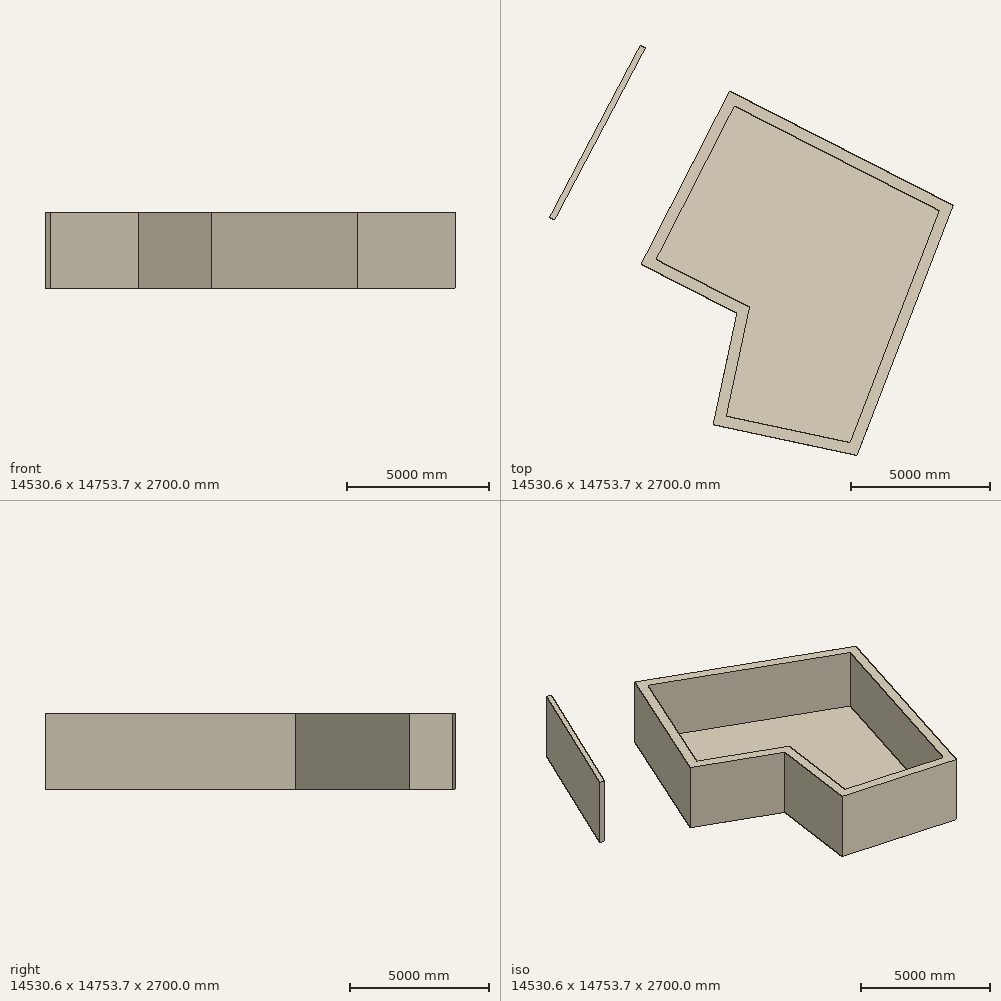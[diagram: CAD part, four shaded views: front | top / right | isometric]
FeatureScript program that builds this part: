
annotation { "Feature Type Name" : "Feature", "Feature Type Description" : "" }
export const myFeature = defineFeature(function(context is Context, id is Id, definition is map)
    precondition{}
    {
        {
            var Q0;
            Q0=qCreatedBy(makeId("Top.planeOp"),FACE);
            var sketch = newSketch(context, id + "F0", { "sketchPlane" : qUnion([Q0])});
            skLineSegment(sketch, "E0", {"start": v(0, 0) * mm, "end": v(-9470, -17950) * mm});
            skLineSegment(sketch, "E1", {"start": v(-9470, -17950) * mm, "end": v(3690, -24620) * mm});
            skLineSegment(sketch, "E2", {"start": v(3690, -24620) * mm, "end": v(11000, -5620) * mm});
            skLineSegment(sketch, "E3", {"start": v(11000, -5620) * mm, "end": v(0, 0) * mm});
            skSolve(sketch);
        }
        {
            var Q0;
            Q0=qCreatedBy(makeId("Top.planeOp"),FACE);
            var sketch = newSketch(context, id + "F1", { "sketchPlane" : qUnion([Q0])});
            skLineSegment(sketch, "E4", {"start": v(-1166.65, -2211.34) * mm, "end": v(10097.33, -7966.2) * mm});
            skLineSegment(sketch, "E5", {"start": v(10097.33, -7966.2) * mm, "end": v(6635.15, -16965.03) * mm});
            skLineSegment(sketch, "E6", {"start": v(6635.15, -16965.03) * mm, "end": v(1452.73, -15857.52) * mm});
            skLineSegment(sketch, "E7", {"start": v(1452.73, -15857.52) * mm, "end": v(2309.57, -11848.05) * mm});
            skLineSegment(sketch, "E8", {"start": v(2309.57, -11848.05) * mm, "end": v(-4433.27, -8403.08) * mm});
            skLineSegment(sketch, "E9", {"start": v(-4433.27, -8403.08) * mm, "end": v(-1166.65, -2211.34) * mm});
            skPoint(sketch, "E10.orphan", {"position": v(0, 0) * mm});
            skLineSegment(sketch, "E11", {"start": v(2048.08, -3853.77) * mm, "end": v(-1136.7, -10087.33) * mm});
            skLineSegment(sketch, "E12", {"start": v(2309.57, -11848.05) * mm, "end": v(3824.07, -4761.14) * mm});
            skLineSegment(sketch, "E13", {"start": v(1271.05, -16707.65) * mm, "end": v(5836.72, -19040.3) * mm});
            skSolve(sketch);
        }
        {
            var Q0;
            Q0=qCreatedBy(makeId("Top.planeOp"),FACE);
            var sketch = newSketch(context, id + "F2", { "sketchPlane" : qUnion([Q0])});
            skLineSegment(sketch, "E14", {"start": v(-1136.7, -10087.33) * mm, "end": v(2048.08, -3853.77) * mm});
            skLineSegment(sketch, "E15", {"start": v(2048.08, -3853.77) * mm, "end": v(10097.33, -7966.2) * mm});
            skLineSegment(sketch, "E16", {"start": v(10097.33, -7966.2) * mm, "end": v(6635.15, -16965.03) * mm});
            skLineSegment(sketch, "E17", {"start": v(6635.15, -16965.03) * mm, "end": v(1452.73, -15857.52) * mm});
            skLineSegment(sketch, "E18", {"start": v(1452.73, -15857.52) * mm, "end": v(2309.57, -11848.05) * mm});
            skLineSegment(sketch, "E19", {"start": v(2309.57, -11848.05) * mm, "end": v(-1136.7, -10087.33) * mm});
            skLineSegment(sketch, "E20", {"start": v(-4433.27, -8403.08) * mm, "end": v(-1166.65, -2211.34) * mm});
            skLineSegment(sketch, "E21", {"start": v(-1166.65, -2211.34) * mm, "end": v(-979.63, -2306.89) * mm});
            skLineSegment(sketch, "E22", {"start": v(-979.63, -2306.89) * mm, "end": v(-4246.24, -8498.63) * mm});
            skLineSegment(sketch, "E23", {"start": v(-4246.24, -8498.63) * mm, "end": v(-4433.27, -8403.08) * mm});
            skSolve(sketch);
        }
        {
            var Q0;
            Q0 = qSketchRegion(id + "F2", true);
            extrude(context, id + "F3", {"entities" : qUnion([Q0]), "oppositeDirection" : true, "depth" : 300 * mm});
        }
        {
            var Q0;
            Q0=qCreatedBy(makeId("Top.planeOp"),FACE);
            var sketch = newSketch(context, id + "F4", { "sketchPlane" : qUnion([Q0])});
            skLineSegment(sketch, "E24.0", {"start": v(2048.08, -3853.77) * mm, "end": v(-1136.7, -10087.33) * mm});
            skLineSegment(sketch, "E25.0", {"start": v(1452.73, -15857.52) * mm, "end": v(2309.57, -11848.05) * mm});
            skPoint(sketch, "E26.0", {"position": v(4043.94, -16411.27) * mm});
            skLineSegment(sketch, "E27.0", {"start": v(6635.15, -16965.03) * mm, "end": v(1452.73, -15857.52) * mm});
            skLineSegment(sketch, "E28.0", {"start": v(10097.33, -7966.2) * mm, "end": v(6635.15, -16965.03) * mm});
            skLineSegment(sketch, "E29.0", {"start": v(-979.63, -2306.89) * mm, "end": v(-4246.24, -8498.63) * mm});
            skLineSegment(sketch, "E30.0", {"start": v(-4433.27, -8403.08) * mm, "end": v(-1166.65, -2211.34) * mm});
            skLineSegment(sketch, "E31", {"start": v(-1166.65, -2211.34) * mm, "end": v(-979.63, -2306.89) * mm});
            skLineSegment(sketch, "E32", {"start": v(-4433.27, -8403.08) * mm, "end": v(-4246.24, -8498.63) * mm});
            skLineSegment(sketch, "E33", {"start": v(-1136.7, -10087.33) * mm, "end": v(2309.57, -11848.05) * mm});
            skLineSegment(sketch, "E34", {"start": v(10097.33, -7966.2) * mm, "end": v(2048.08, -3853.77) * mm});
            skLineSegment(sketch, "E35.0", {"start": v(9594.72, -8158.6) * mm, "end": v(2222.3, -4391.96) * mm});
            skLineSegment(sketch, "E35.1", {"start": v(-598.5, -9913.1) * mm, "end": v(2764.88, -11631.5) * mm});
            skLineSegment(sketch, "E35.2", {"start": v(1927.5, -15549.95) * mm, "end": v(2764.88, -11631.5) * mm});
            skLineSegment(sketch, "E35.3", {"start": v(2222.3, -4391.96) * mm, "end": v(-598.5, -9913.1) * mm});
            skLineSegment(sketch, "E35.4", {"start": v(6384.54, -16502.44) * mm, "end": v(1927.5, -15549.95) * mm});
            skLineSegment(sketch, "E35.5", {"start": v(9594.72, -8158.6) * mm, "end": v(6384.54, -16502.44) * mm});
            skSolve(sketch);
        }
        {
            var Q0;
            Q0 = qSketchRegion(id + "F4", true);
            extrude(context, id + "F5", {"entities" : qUnion([Q0]), "operationType" : NewBodyOperationType.ADD, "depth" : 2400 * mm});
        }
    });
